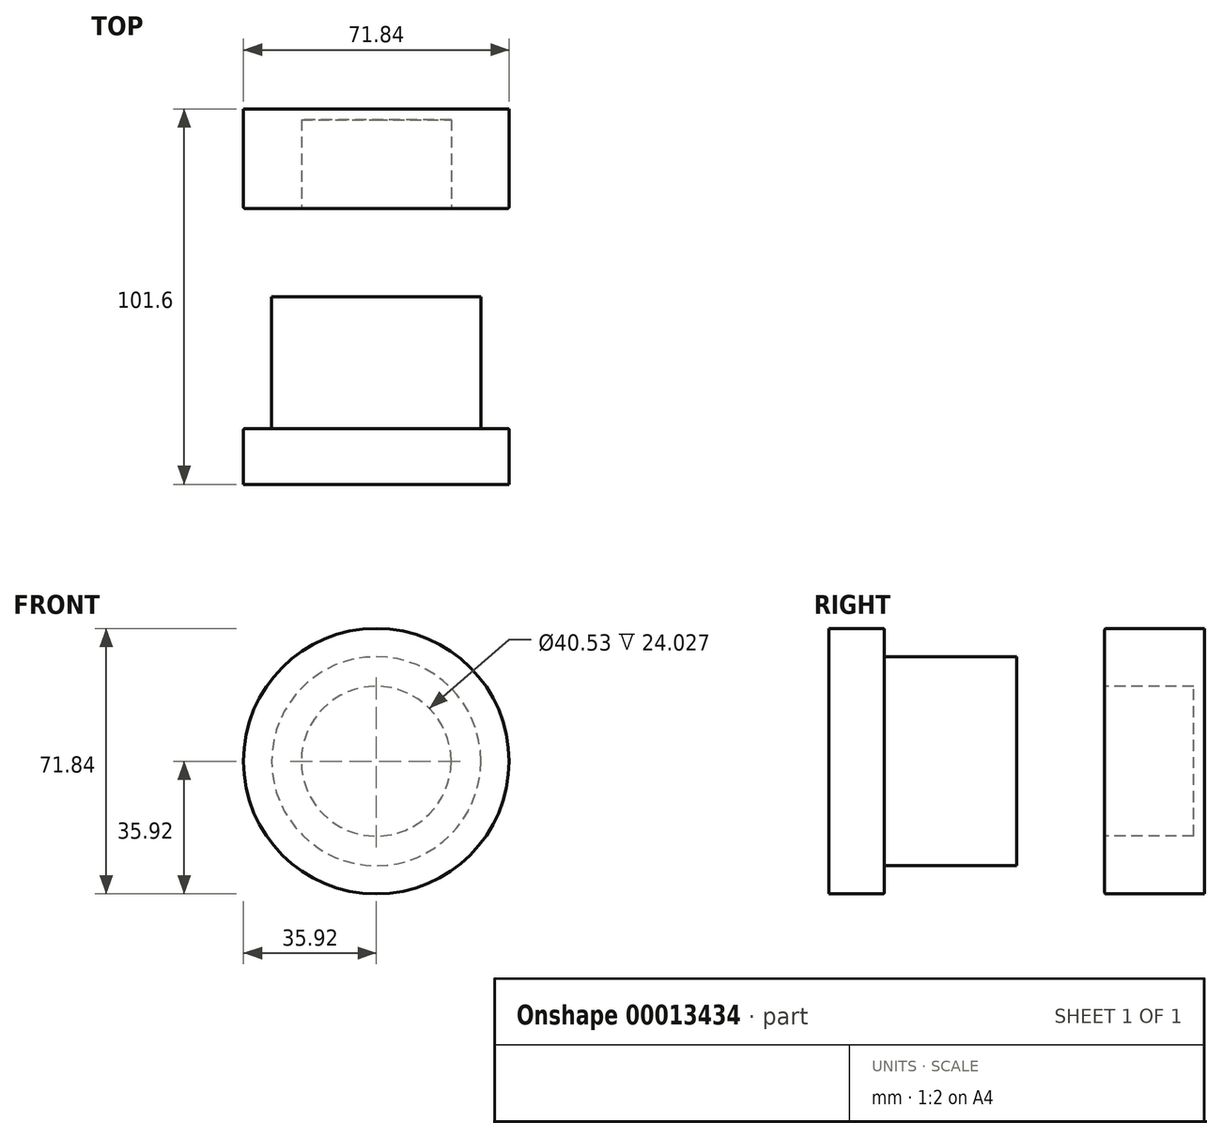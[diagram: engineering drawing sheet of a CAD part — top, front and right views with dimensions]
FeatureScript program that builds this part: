
annotation { "Feature Type Name" : "Feature", "Feature Type Description" : "" }
export const myFeature = defineFeature(function(context is Context, id is Id, definition is map)
    precondition{}
    {
        {
            var Q0;
            Q0=qCreatedBy(makeId("Front.planeOp"),FACE);
            var sketch = newSketch(context, id + "F0", { "sketchPlane" : qUnion([Q0])});
            skCircle(sketch, "E0", {"center": v(0, 0) * mm, "radius": 35.92 * mm});
            skSolve(sketch);
        }
        {
            var Q0;
            Q0=makeQuery(id+"F0.imprint","IMPRINT",FACE,{"disambiguationData":[TD([[makeQuery(id+"F0.imprint","IMPRINT",EDGE,{"derivedFrom":sQuery(id+"F0.wireOp",EDGE,"E0")}),1.0]])]});
            extrude(context, id + "F1", {"entities" : qUnion([Q0]), "endBound" : BoundingType.SYMMETRIC, "oppositeDirection" : true, "depth" : 101.6 * mm});
        }
        {
            var Q0;
            Q0=qCreatedBy(makeId("Right.planeOp"),FACE);
            var sketch = newSketch(context, id + "F2", { "sketchPlane" : qUnion([Q0])});
            skLineSegment(sketch, "E1.bottom", {"start": v(0, 0) * mm, "end": v(23.87, 0) * mm});
            skLineSegment(sketch, "E1.top", {"start": v(0, 37.08) * mm, "end": v(23.87, 37.08) * mm});
            skLineSegment(sketch, "E1.left", {"start": v(0, 0) * mm, "end": v(0, 37.08) * mm});
            skLineSegment(sketch, "E1.right", {"start": v(23.87, 0) * mm, "end": v(23.87, 37.08) * mm});
            skLineSegment(sketch, "E2.bottom", {"start": v(23.87, 20.26) * mm, "end": v(47.9, 20.26) * mm});
            skLineSegment(sketch, "E2.top", {"start": v(23.87, 0) * mm, "end": v(47.9, 0) * mm});
            skLineSegment(sketch, "E2.left", {"start": v(23.87, 20.26) * mm, "end": v(23.87, 0) * mm});
            skLineSegment(sketch, "E2.right", {"start": v(47.9, 20.26) * mm, "end": v(47.9, 0) * mm});
            skLineSegment(sketch, "E3.bottom", {"start": v(0, 37.08) * mm, "end": v(-35.72, 37.08) * mm});
            skLineSegment(sketch, "E3.top", {"start": v(0, 28.27) * mm, "end": v(-35.72, 28.27) * mm});
            skLineSegment(sketch, "E3.left", {"start": v(0, 37.08) * mm, "end": v(0, 28.27) * mm});
            skLineSegment(sketch, "E3.right", {"start": v(-35.72, 37.08) * mm, "end": v(-35.72, 28.27) * mm});
            skLineSegment(sketch, "E4", {"start": v(0, 0) * mm, "end": v(-52.54, 0) * mm});
            skSolve(sketch);
        }
        {
            var Q0;
            Q0 = qSketchRegion(id + "F2", true);
            var Q1;
            Q1=makeQuery(id+"F1.opExtrude","CAP_EDGE",EDGE,{"disambiguationData":[OSD([sQuery(id+"F0.wireOp",EDGE,"E0")])],"isStart":false});
            revolve(context, id + "F3", {"operationType" : NewBodyOperationType.REMOVE, "entities" : qUnion([Q0]), "axis" : qUnion([Q1]), "revolveType" : RevolveType.FULL, "oppositeDirection" : true});
        }
        {
            var Q0;
            Q0=makeQuery(id+"F3.boolean.opBoolean","INTERSECT",EDGE,{"derivedFrom":[makeQuery(id+"F1.opExtrude","SWEPT_FACE",FACE,{"disambiguationData":[OSD([sQuery(id+"F0.wireOp",EDGE,"E0")])]}),makeQuery(id+"F3.opRevolve","SWEPT_FACE",FACE,{"disambiguationData":[OSD([sQuery(id+"F2.wireOp",EDGE,"E3.right")])]})]});
            var Q1;
            Q1=makeQuery(id+"F3.boolean.opBoolean","INTERSECT",EDGE,{"derivedFrom":[makeQuery(id+"F1.opExtrude","SWEPT_FACE",FACE,{"disambiguationData":[OSD([sQuery(id+"F0.wireOp",EDGE,"E0")])]}),makeQuery(id+"F3.opRevolve","SWEPT_FACE",FACE,{"disambiguationData":[OSD([sQuery(id+"F2.wireOp",EDGE,"E1.right")])]})]});
            fillet(context, id + "F4", {"entities" : qUnion([Q0, Q1]), "radius" : 0.4 * mm, "tangentPropagation" : true, "allowEdgeOverflow" : false});
        }
    });
